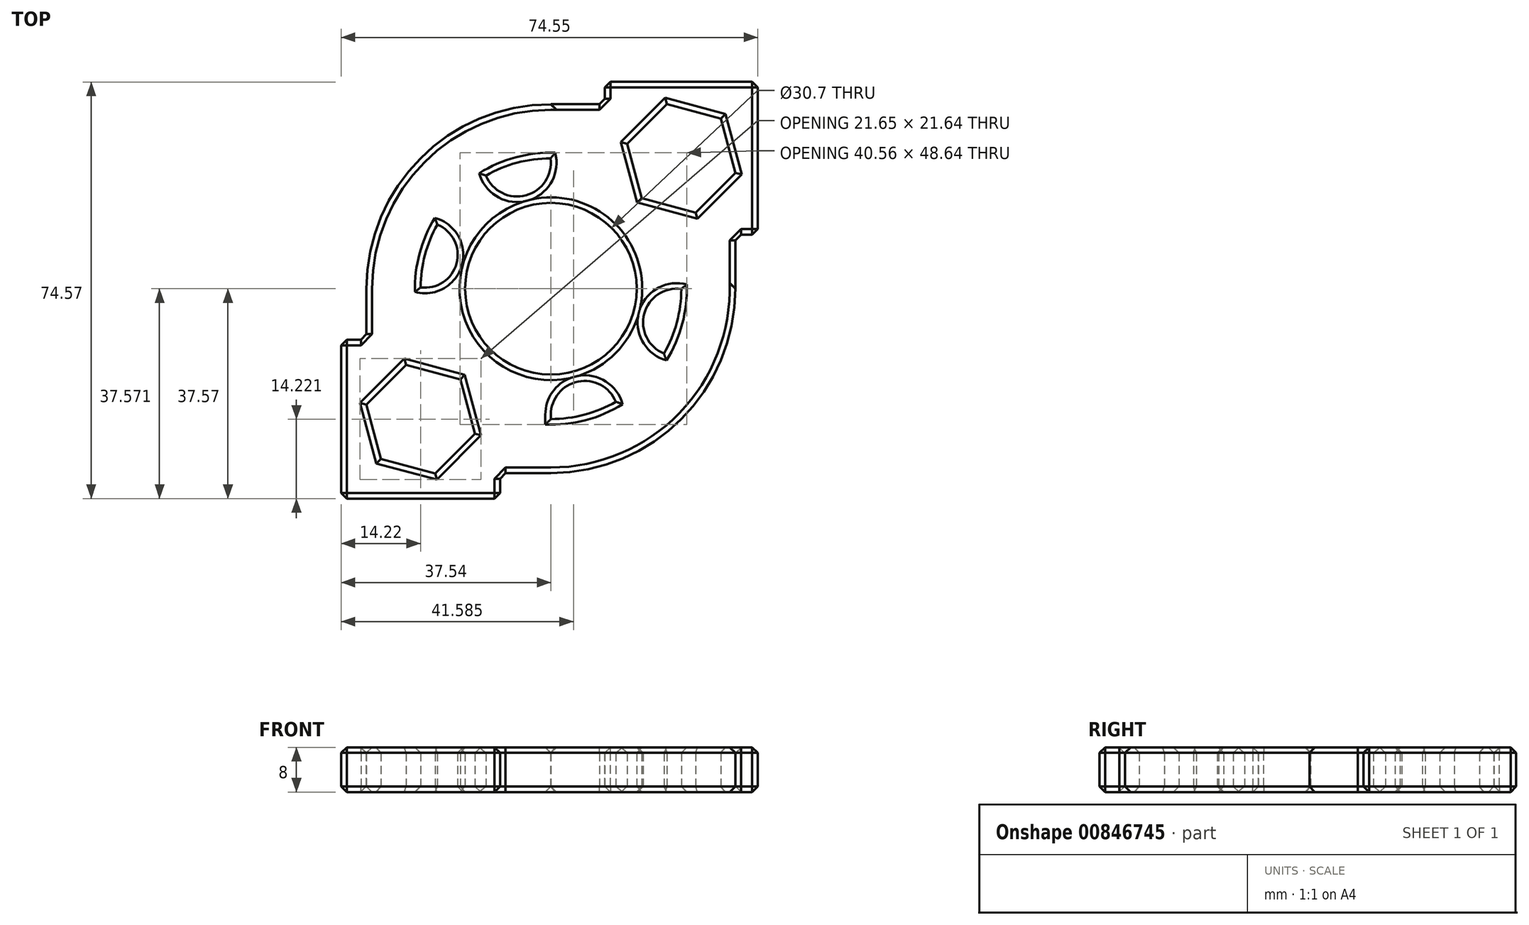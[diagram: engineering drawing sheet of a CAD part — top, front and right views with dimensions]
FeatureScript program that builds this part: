
annotation { "Feature Type Name" : "Feature", "Feature Type Description" : "" }
export const myFeature = defineFeature(function(context is Context, id is Id, definition is map)
    precondition{}
    {
        {
            var Q0;
            Q0=qCreatedBy(makeId("Top.planeOp"),FACE);
            var sketch = newSketch(context, id + "F0", { "sketchPlane" : qUnion([Q0])});
            skCircle(sketch, "E0", {"center": v(0, 0) * mm, "radius": 15.35 * mm});
            skLineSegment(sketch, "E1", {"start": v(0, -33) * mm, "end": v(0, -20.33) * mm});
            skLineSegment(sketch, "E2", {"start": v(0, 16.5) * mm, "end": v(0, 16.5) * mm});
            skCircle(sketch, "E3.cCircle", {"center": v(16.5, 16.5) * mm, "radius": 9.67 * mm, "construction": true});
            skLineSegment(sketch, "E3.0", {"start": v(0, 23.33) * mm, "end": v(0, 33) * mm});
            skLineSegment(sketch, "E3.2", {"start": v(26.17, 16.5) * mm, "end": v(26.17, 16.5) * mm});
            skCircle(sketch, "E4.cCircle", {"center": v(23.34, 23.33) * mm, "radius": 9.67 * mm, "construction": true});
            skLineSegment(sketch, "E4.0", {"start": v(16.5, 26.16) * mm, "end": v(16.5, 26.17) * mm});
            skLineSegment(sketch, "E4.2", {"start": v(30.17, 16.5) * mm, "end": v(30.17, 16.5) * mm});
            skArc(sketch, "E5.cCircle", {"start": v(20.23, -11.62) * mm, "mid": v(-16.5, 16.5) * mm, "end": v(11.62, -20.23) * mm, "construction": true});
            skLineSegment(sketch, "E5.0", {"start": v(16.5, 16.5) * mm, "end": v(16.5, 16.5) * mm});
            skLineSegment(sketch, "E5.1", {"start": v(6.83, -16.5) * mm, "end": v(6.04, -16.5) * mm});
            skCircle(sketch, "E6.cCircle", {"center": v(-16.5, -16.5) * mm, "radius": 23.33 * mm, "construction": true});
            skLineSegment(sketch, "E6.0", {"start": v(0, -20.33) * mm, "end": v(0, -33) * mm});
            skLineSegment(sketch, "E6.1", {"start": v(0, -33) * mm, "end": v(-6.69, -33) * mm});
            skLineSegment(sketch, "E6.3", {"start": v(-33, 0) * mm, "end": v(-23.33, 0) * mm});
            skCircle(sketch, "E7.cCircle", {"center": v(-33.17, -33.43) * mm, "radius": 23.76 * mm, "construction": true});
            skLineSegment(sketch, "E7.0", {"start": v(-16.32, -39.83) * mm, "end": v(-16.32, -39.97) * mm});
            skCircle(sketch, "E8.cCircle", {"center": v(-23.32, -23.35) * mm, "radius": 10.05 * mm, "construction": true});
            skLineSegment(sketch, "E8.0", {"start": v(-16.22, -16.24) * mm, "end": v(-13.61, -25.94) * mm});
            skLineSegment(sketch, "E8.1", {"start": v(-13.61, -25.94) * mm, "end": v(-20.71, -33.05) * mm});
            skLineSegment(sketch, "E8.2", {"start": v(-20.71, -33.05) * mm, "end": v(-30.42, -30.46) * mm});
            skLineSegment(sketch, "E8.3", {"start": v(-30.42, -30.46) * mm, "end": v(-33.03, -20.75) * mm});
            skLineSegment(sketch, "E8.4", {"start": v(-33.03, -20.75) * mm, "end": v(-25.93, -13.64) * mm});
            skLineSegment(sketch, "E8.5", {"start": v(-25.93, -13.64) * mm, "end": v(-16.22, -16.24) * mm});
            skCircle(sketch, "E9.cCircle", {"center": v(23.34, 23.33) * mm, "radius": 10.05 * mm, "construction": true});
            skLineSegment(sketch, "E9.0", {"start": v(16.23, 16.23) * mm, "end": v(13.63, 25.94) * mm});
            skLineSegment(sketch, "E9.1", {"start": v(13.63, 25.94) * mm, "end": v(20.74, 33.04) * mm});
            skLineSegment(sketch, "E9.2", {"start": v(20.74, 33.04) * mm, "end": v(30.44, 30.44) * mm});
            skLineSegment(sketch, "E9.3", {"start": v(30.44, 30.44) * mm, "end": v(33.04, 20.73) * mm});
            skLineSegment(sketch, "E9.4", {"start": v(33.04, 20.73) * mm, "end": v(25.93, 13.62) * mm});
            skLineSegment(sketch, "E9.5", {"start": v(25.93, 13.62) * mm, "end": v(16.23, 16.23) * mm});
            skLineSegment(sketch, "E10.trimOffspring", {"start": v(-33, -6.73) * mm, "end": v(-33, 0) * mm});
            skArc(sketch, "E11.cCircle", {"start": v(-23.33, 0.17) * mm, "mid": v(-27.39, -46.5) * mm, "end": v(-15.3, -1.24) * mm, "construction": true});
            skLineSegment(sketch, "E11.1", {"start": v(-10.33, -39.97) * mm, "end": v(-39.94, -39.99) * mm});
            skLineSegment(sketch, "E11.2", {"start": v(-39.94, -39.99) * mm, "end": v(-39.96, -6.73) * mm});
            skLineSegment(sketch, "E11.3", {"start": v(-39.96, -6.73) * mm, "end": v(-33, -6.73) * mm});
            skLineSegment(sketch, "E12.trimOffspring", {"start": v(-39.95, -16.68) * mm, "end": v(-39.83, -16.68) * mm});
            skLineSegment(sketch, "E13.trimOffspring", {"start": v(-16.22, -16.24) * mm, "end": v(-16.22, -16.24) * mm});
            skPoint(sketch, "E14.orphan", {"position": v(-6.7, -6.71) * mm});
            skLineSegment(sketch, "E15.trimOffspring", {"start": v(16.23, 16.23) * mm, "end": v(16.23, 16.23) * mm});
            skPoint(sketch, "E16.orphan", {"position": v(30.17, 30.17) * mm});
            skCircle(sketch, "E17.cCircle", {"center": v(16.5, 16.5) * mm, "radius": 23.34 * mm, "construction": true});
            skLineSegment(sketch, "E17.0", {"start": v(0, 33) * mm, "end": v(0, 33) * mm});
            skLineSegment(sketch, "E17.1", {"start": v(0, 33) * mm, "end": v(9.67, 33) * mm});
            skLineSegment(sketch, "E17.3", {"start": v(33, 0) * mm, "end": v(33, 0) * mm});
            skCircle(sketch, "E18.cCircle", {"center": v(23.34, 23.33) * mm, "radius": 19.33 * mm, "construction": true});
            skLineSegment(sketch, "E18.1", {"start": v(9.67, 37) * mm, "end": v(37, 37) * mm});
            skLineSegment(sketch, "E18.2", {"start": v(37, 37) * mm, "end": v(37, 9.66) * mm});
            skLineSegment(sketch, "E18.3", {"start": v(37, 9.66) * mm, "end": v(33, 9.66) * mm});
            skPoint(sketch, "E19.orphan", {"position": v(9.67, 9.66) * mm});
            skLineSegment(sketch, "E20.trimOffspring", {"start": v(33, 9.66) * mm, "end": v(33, 0) * mm});
            skPoint(sketch, "E21.orphan", {"position": v(33, 16.5) * mm});
            skLineSegment(sketch, "E22.trimOffspring", {"start": v(9.67, 33) * mm, "end": v(9.67, 37) * mm});
            skLineSegment(sketch, "E23.trimOffspring", {"start": v(16.5, 26.17) * mm, "end": v(16.5, 26.16) * mm});
            skPoint(sketch, "E24.orphan", {"position": v(33, 33) * mm});
            skLineSegment(sketch, "E25.trimOffspring", {"start": v(16.5, 0) * mm, "end": v(16.5, 0) * mm});
            skCircle(sketch, "E26", {"center": v(0, 0) * mm, "radius": 23.33 * mm});
            skArc(sketch, "E27", {"start": v(-1.85, -32.95) * mm, "mid": v(22, 24.6) * mm, "end": v(-32.54, -5.49) * mm});
            skCircle(sketch, "E28", {"center": v(-6.04, 22.54) * mm, "radius": 6.04 * mm});
            skArc(sketch, "E29", {"start": v(-23.33, 0.23) * mm, "mid": v(-16.87, 4.52) * mm, "end": v(-20.32, 11.47) * mm});
            skArc(sketch, "E30", {"start": v(23.33, -0.06) * mm, "mid": v(16.7, -4.48) * mm, "end": v(20.23, -11.62) * mm});
            skArc(sketch, "E31", {"start": v(11.62, -20.23) * mm, "mid": v(1.77, -18.27) * mm, "end": v(3.73, -28.12) * mm});
            skPoint(sketch, "E32.orphan", {"position": v(16.5, -16.5) * mm});
            skPoint(sketch, "E33.orphan", {"position": v(-16.5, 16.5) * mm});
            skLineSegment(sketch, "E34.trimOffspring", {"start": v(0, 22.65) * mm, "end": v(0, 22.43) * mm});
            skPoint(sketch, "E35.start.orphan", {"position": v(0, 33) * mm});
            skCircle(sketch, "E36", {"center": v(-16.22, -16.24) * mm, "radius": 10.05 * mm});
            skLineSegment(sketch, "E37", {"start": v(-6.7, -6.71) * mm, "end": v(-16.22, -16.24) * mm});
            skCircle(sketch, "E38.cCircle", {"center": v(-23.32, -23.35) * mm, "radius": 20.1 * mm, "construction": true});
            skLineSegment(sketch, "E38.0", {"start": v(-9.12, -9.13) * mm, "end": v(-9.1, -23.34) * mm});
            skLineSegment(sketch, "E38.1", {"start": v(-9.1, -37.55) * mm, "end": v(-37.53, -37.57) * mm});
            skLineSegment(sketch, "E38.2", {"start": v(-37.53, -37.57) * mm, "end": v(-37.54, -9.14) * mm});
            skLineSegment(sketch, "E38.3", {"start": v(-37.54, -9.14) * mm, "end": v(-9.12, -9.13) * mm});
            skLineSegment(sketch, "E39", {"start": v(-33, -6.73) * mm, "end": v(-33, -9.14) * mm});
            skLineSegment(sketch, "E40", {"start": v(-6.69, -33) * mm, "end": v(-9.12, -33) * mm});
            skLineSegment(sketch, "E41.trimOffspring", {"start": v(-9.1, -33) * mm, "end": v(-9.1, -37.55) * mm});
            skPoint(sketch, "E42.orphan", {"position": v(-6.68, -39.97) * mm});
            skArc(sketch, "E43.trimOffspring", {"start": v(-31.7, -9.14) * mm, "mid": v(-25.53, -20.9) * mm, "end": v(-15.21, -29.29) * mm});
            skSolve(sketch);
        }
        {
            var Q0;
            {var subQ3=sQuery(id+"F0.wireOp",EDGE,"E8.0");var subQ5=sQuery(id+"F0.wireOp",EDGE,"E8.1");var subQ6=makeQuery(id+"F0.imprint","INTERSECT",VERTEX,{"derivedFrom":[subQ3,subQ5]});Q0=makeQuery(id+"F0.imprint","IMPRINT",FACE,{"disambiguationData":[TD([[makeQuery(id+"F0.imprint","IMPRINT",EDGE,{"disambiguationData":[TD([[subQ6,1.0]])],"derivedFrom":subQ3}),1.0]])]});}
            var Q1;
            {var subQ4=sQuery(id+"F0.wireOp",EDGE,"E27");var subQ5=sQuery(id+"F0.wireOp",EDGE,"E3.0");var subQ6=makeQuery(id+"F0.imprint","INTERSECT",VERTEX,{"derivedFrom":[subQ5,subQ4]});Q1=makeQuery(id+"F0.imprint","IMPRINT",FACE,{"disambiguationData":[TD([[makeQuery(id+"F0.imprint","IMPRINT",EDGE,{"disambiguationData":[TD([[subQ6,1.0]])],"derivedFrom":subQ5}),1.0]])]});}
            var Q2;
            {var subQ1=sQuery(id+"F0.wireOp",EDGE,"E9.0");var subQ7=sQuery(id+"F0.wireOp",EDGE,"E9.1");var subQ9=makeQuery(id+"F0.imprint","INTERSECT",VERTEX,{"derivedFrom":[subQ1,subQ7]});Q2=makeQuery(id+"F0.imprint","IMPRINT",FACE,{"disambiguationData":[TD([[makeQuery(id+"F0.imprint","IMPRINT",EDGE,{"disambiguationData":[TD([[subQ9,1.0]])],"derivedFrom":subQ1}),1.0]])]});}
            var Q3;
            {var subQ4=sQuery(id+"F0.wireOp",EDGE,"E6.1");Q3=makeQuery(id+"F0.imprint","IMPRINT",FACE,{"disambiguationData":[TD([[makeQuery(id+"F0.imprint","IMPRINT",EDGE,{"derivedFrom":subQ4}),-1.0]])]});}
            var Q4;
            {var subQ7=sQuery(id+"F0.wireOp",EDGE,"E9.2");Q4=makeQuery(id+"F0.imprint","IMPRINT",FACE,{"disambiguationData":[TD([[makeQuery(id+"F0.imprint","IMPRINT",EDGE,{"derivedFrom":subQ7}),1.0]])]});}
            var Q5;
            {var subQ4=sQuery(id+"F0.wireOp",EDGE,"E17.3");var subQ6=sQuery(id+"F0.wireOp",EDGE,"E27");var subQ8=makeQuery(id+"F0.imprint","INTERSECT",VERTEX,{"derivedFrom":[subQ4,subQ6]});Q5=makeQuery(id+"F0.imprint","IMPRINT",FACE,{"disambiguationData":[TD([[makeQuery(id+"F0.imprint","IMPRINT",EDGE,{"disambiguationData":[TD([[subQ8,-1.0]])],"derivedFrom":subQ4}),1.0]])]});}
            var Q6;
            {var subQ5=sQuery(id+"F0.wireOp",EDGE,"E27");var subQ7=sQuery(id+"F0.wireOp",EDGE,"E3.3");var subQ9=makeQuery(id+"F0.imprint","INTERSECT",VERTEX,{"derivedFrom":[subQ7,subQ5]});Q6=makeQuery(id+"F0.imprint","IMPRINT",FACE,{"disambiguationData":[TD([[makeQuery(id+"F0.imprint","IMPRINT",EDGE,{"disambiguationData":[TD([[subQ9,-1.0]])],"derivedFrom":subQ7}),-1.0]])]});}
            var Q7;
            Q7=makeQuery(id+"F0.imprint","IMPRINT",FACE,{"disambiguationData":[TD([[makeQuery(id+"F0.imprint","IMPRINT",EDGE,{"derivedFrom":sQuery(id+"F0.wireOp",EDGE,"E0")}),-1.0]])]});
            var Q8;
            {var subQ0=sQuery(id+"F0.wireOp",EDGE,"E28");var subQ1=sQuery(id+"F0.wireOp",EDGE,"E26");var subQ2=makeQuery(id+"F0.imprint","INTERSECT",VERTEX,{"disambiguationData":[OD(0.0)],"derivedFrom":[subQ1,subQ0]});Q8=makeQuery(id+"F0.imprint","IMPRINT",FACE,{"disambiguationData":[TD([[makeQuery(id+"F0.imprint","IMPRINT",EDGE,{"disambiguationData":[TD([[subQ2,-1.0]])],"derivedFrom":subQ1}),-1.0]])]});}
            var Q9;
            {var subQ0=sQuery(id+"F0.wireOp",EDGE,"E9.5");var subQ1=sQuery(id+"F0.wireOp",EDGE,"E9.4");var subQ2=makeQuery(id+"F0.imprint","INTERSECT",VERTEX,{"derivedFrom":[subQ1,subQ0]});Q9=makeQuery(id+"F0.imprint","IMPRINT",FACE,{"disambiguationData":[TD([[makeQuery(id+"F0.imprint","IMPRINT",EDGE,{"disambiguationData":[TD([[subQ2,1.0]])],"derivedFrom":subQ1}),1.0]])]});}
            var Q10;
            {var subQ3=sQuery(id+"F0.wireOp",EDGE,"E43.trimOffspring");var subQ5=sQuery(id+"F0.wireOp",EDGE,"E38.3");var subQ7=makeQuery(id+"F0.imprint","INTERSECT",VERTEX,{"derivedFrom":[subQ5,subQ3]});Q10=makeQuery(id+"F0.imprint","IMPRINT",FACE,{"disambiguationData":[TD([[makeQuery(id+"F0.imprint","IMPRINT",EDGE,{"disambiguationData":[TD([[subQ7,-1.0]])],"derivedFrom":subQ5}),-1.0]])]});}
            var Q11;
            {var subQ1=sQuery(id+"F0.wireOp",EDGE,"E8.5");var subQ3=sQuery(id+"F0.wireOp",EDGE,"E26");var subQ4=makeQuery(id+"F0.imprint","INTERSECT",VERTEX,{"derivedFrom":[subQ1,subQ3]});Q11=makeQuery(id+"F0.imprint","IMPRINT",FACE,{"disambiguationData":[TD([[makeQuery(id+"F0.imprint","IMPRINT",EDGE,{"disambiguationData":[TD([[subQ4,1.0]])],"derivedFrom":subQ3}),-1.0]])]});}
            var Q12;
            {var subQ1=sQuery(id+"F0.wireOp",EDGE,"E6.3");Q12=makeQuery(id+"F0.imprint","IMPRINT",FACE,{"disambiguationData":[TD([[makeQuery(id+"F0.imprint","IMPRINT",EDGE,{"derivedFrom":subQ1}),-1.0]])]});}
            var Q13;
            {var subQ0=sQuery(id+"F0.wireOp",EDGE,"E36");var subQ1=sQuery(id+"F0.wireOp",EDGE,"E26");var subQ2=makeQuery(id+"F0.imprint","INTERSECT",VERTEX,{"disambiguationData":[OD(0.0)],"derivedFrom":[subQ1,subQ0]});Q13=makeQuery(id+"F0.imprint","IMPRINT",FACE,{"disambiguationData":[TD([[makeQuery(id+"F0.imprint","IMPRINT",EDGE,{"disambiguationData":[TD([[subQ2,-1.0]])],"derivedFrom":subQ1}),-1.0]])]});}
            var Q14;
            {var subQ0=sQuery(id+"F0.wireOp",EDGE,"E38.0");var subQ1=sQuery(id+"F0.wireOp",EDGE,"E26");var subQ2=makeQuery(id+"F0.imprint","INTERSECT",VERTEX,{"derivedFrom":[subQ1,subQ0]});Q14=makeQuery(id+"F0.imprint","IMPRINT",FACE,{"disambiguationData":[TD([[makeQuery(id+"F0.imprint","IMPRINT",EDGE,{"disambiguationData":[TD([[subQ2,-1.0]])],"derivedFrom":subQ1}),-1.0]])]});}
            var Q15;
            {var subQ0=sQuery(id+"F0.wireOp",EDGE,"E37");var subQ3=sQuery(id+"F0.wireOp",EDGE,"E0");var subQ4=makeQuery(id+"F0.imprint","INTERSECT",VERTEX,{"derivedFrom":[subQ3,subQ0]});Q15=makeQuery(id+"F0.imprint","IMPRINT",FACE,{"disambiguationData":[TD([[makeQuery(id+"F0.imprint","IMPRINT",EDGE,{"disambiguationData":[TD([[subQ4,-1.0]])],"derivedFrom":subQ3}),-1.0]])]});}
            var Q16;
            {var subQ0=sQuery(id+"F0.wireOp",EDGE,"E8.5");var subQ1=makeQuery(id+"F0.imprint","IMPRINT",VERTEX,{"derivedFrom":subQ0});Q16=makeQuery(id+"F0.imprint","IMPRINT",FACE,{"disambiguationData":[TD([[makeQuery(id+"F0.imprint","IMPRINT",EDGE,{"disambiguationData":[TD([[subQ1,1.0]])],"derivedFrom":subQ0}),1.0]])]});}
            var Q17;
            {var subQ10=sQuery(id+"F0.wireOp",EDGE,"E29");Q17=makeQuery(id+"F0.imprint","IMPRINT",FACE,{"disambiguationData":[TD([[makeQuery(id+"F0.imprint","IMPRINT",EDGE,{"derivedFrom":subQ10}),-1.0]])]});}
            extrude(context, id + "F1", {"entities" : qUnion([Q0, Q1, Q2, Q3, Q4, Q5, Q6, Q7, Q8, Q9, Q10, Q11, Q12, Q13, Q14, Q15, Q16, Q17]), "depth" : 8 * mm, "offsetDistance" : 25 * mm});
        }
        {
            var Q0;
            Q0=makeQuery(id+"F1.opExtrude","CAP_FACE",FACE,{"disambiguationData":[OSD([sQuery(id+"F0.wireOp",EDGE,"E0"),sQuery(id+"F0.wireOp",EDGE,"E6.0"),sQuery(id+"F0.wireOp",EDGE,"E6.1"),sQuery(id+"F0.wireOp",EDGE,"E8.0"),sQuery(id+"F0.wireOp",EDGE,"E8.1"),sQuery(id+"F0.wireOp",EDGE,"E8.2"),sQuery(id+"F0.wireOp",EDGE,"E8.3"),sQuery(id+"F0.wireOp",EDGE,"E8.4"),sQuery(id+"F0.wireOp",EDGE,"E8.5"),sQuery(id+"F0.wireOp",EDGE,"E9.0"),sQuery(id+"F0.wireOp",EDGE,"E9.1"),sQuery(id+"F0.wireOp",EDGE,"E9.2"),sQuery(id+"F0.wireOp",EDGE,"E9.3"),sQuery(id+"F0.wireOp",EDGE,"E9.4"),sQuery(id+"F0.wireOp",EDGE,"E9.5"),sQuery(id+"F0.wireOp",EDGE,"E10.trimOffspring"),sQuery(id+"F0.wireOp",EDGE,"E17.0"),sQuery(id+"F0.wireOp",EDGE,"E17.1"),sQuery(id+"F0.wireOp",EDGE,"E17.3"),sQuery(id+"F0.wireOp",EDGE,"E18.1"),sQuery(id+"F0.wireOp",EDGE,"E18.2"),sQuery(id+"F0.wireOp",EDGE,"E18.3"),sQuery(id+"F0.wireOp",EDGE,"E20.trimOffspring"),sQuery(id+"F0.wireOp",EDGE,"E22.trimOffspring"),sQuery(id+"F0.wireOp",EDGE,"E26"),sQuery(id+"F0.wireOp",EDGE,"E27"),sQuery(id+"F0.wireOp",EDGE,"E28"),sQuery(id+"F0.wireOp",EDGE,"E29"),sQuery(id+"F0.wireOp",EDGE,"E30"),sQuery(id+"F0.wireOp",EDGE,"E31"),sQuery(id+"F0.wireOp",EDGE,"E38.1"),sQuery(id+"F0.wireOp",EDGE,"E38.2"),sQuery(id+"F0.wireOp",EDGE,"E38.3"),sQuery(id+"F0.wireOp",EDGE,"E39"),sQuery(id+"F0.wireOp",EDGE,"E40"),sQuery(id+"F0.wireOp",EDGE,"E41.trimOffspring")])],"isStart":true});
            var Q1;
            Q1=makeQuery(id+"F1.opExtrude","CAP_FACE",FACE,{"disambiguationData":[OSD([sQuery(id+"F0.wireOp",EDGE,"E0"),sQuery(id+"F0.wireOp",EDGE,"E6.0"),sQuery(id+"F0.wireOp",EDGE,"E6.1"),sQuery(id+"F0.wireOp",EDGE,"E8.0"),sQuery(id+"F0.wireOp",EDGE,"E8.1"),sQuery(id+"F0.wireOp",EDGE,"E8.2"),sQuery(id+"F0.wireOp",EDGE,"E8.3"),sQuery(id+"F0.wireOp",EDGE,"E8.4"),sQuery(id+"F0.wireOp",EDGE,"E8.5"),sQuery(id+"F0.wireOp",EDGE,"E9.0"),sQuery(id+"F0.wireOp",EDGE,"E9.1"),sQuery(id+"F0.wireOp",EDGE,"E9.2"),sQuery(id+"F0.wireOp",EDGE,"E9.3"),sQuery(id+"F0.wireOp",EDGE,"E9.4"),sQuery(id+"F0.wireOp",EDGE,"E9.5"),sQuery(id+"F0.wireOp",EDGE,"E10.trimOffspring"),sQuery(id+"F0.wireOp",EDGE,"E17.0"),sQuery(id+"F0.wireOp",EDGE,"E17.1"),sQuery(id+"F0.wireOp",EDGE,"E17.3"),sQuery(id+"F0.wireOp",EDGE,"E18.1"),sQuery(id+"F0.wireOp",EDGE,"E18.2"),sQuery(id+"F0.wireOp",EDGE,"E18.3"),sQuery(id+"F0.wireOp",EDGE,"E20.trimOffspring"),sQuery(id+"F0.wireOp",EDGE,"E22.trimOffspring"),sQuery(id+"F0.wireOp",EDGE,"E26"),sQuery(id+"F0.wireOp",EDGE,"E27"),sQuery(id+"F0.wireOp",EDGE,"E28"),sQuery(id+"F0.wireOp",EDGE,"E29"),sQuery(id+"F0.wireOp",EDGE,"E30"),sQuery(id+"F0.wireOp",EDGE,"E31"),sQuery(id+"F0.wireOp",EDGE,"E38.1"),sQuery(id+"F0.wireOp",EDGE,"E38.2"),sQuery(id+"F0.wireOp",EDGE,"E38.3"),sQuery(id+"F0.wireOp",EDGE,"E39"),sQuery(id+"F0.wireOp",EDGE,"E40"),sQuery(id+"F0.wireOp",EDGE,"E41.trimOffspring")])],"isStart":false});
            var Q2;
            Q2=makeQuery(id+"F1.opExtrude","SWEPT_EDGE",EDGE,{"disambiguationData":[OSD([sQuery(id+"F0.wireOp",EDGE,"E18.1"),sQuery(id+"F0.wireOp",EDGE,"E18.2")])]});
            var Q3;
            Q3=makeQuery(id+"F1.opExtrude","SWEPT_EDGE",EDGE,{"disambiguationData":[OSD([sQuery(id+"F0.wireOp",EDGE,"E18.1"),sQuery(id+"F0.wireOp",EDGE,"E22.trimOffspring")])]});
            var Q4;
            Q4=makeQuery(id+"F1.opExtrude","SWEPT_EDGE",EDGE,{"disambiguationData":[OSD([sQuery(id+"F0.wireOp",EDGE,"E17.1"),sQuery(id+"F0.wireOp",EDGE,"E22.trimOffspring")])]});
            var Q5;
            Q5=makeQuery(id+"F1.opExtrude","SWEPT_EDGE",EDGE,{"disambiguationData":[OSD([sQuery(id+"F0.wireOp",EDGE,"E18.3"),sQuery(id+"F0.wireOp",EDGE,"E20.trimOffspring")])]});
            var Q6;
            Q6=makeQuery(id+"F1.opExtrude","SWEPT_EDGE",EDGE,{"disambiguationData":[OSD([sQuery(id+"F0.wireOp",EDGE,"E18.2"),sQuery(id+"F0.wireOp",EDGE,"E18.3")])]});
            var Q7;
            Q7=makeQuery(id+"F1.opExtrude","SWEPT_EDGE",EDGE,{"disambiguationData":[OSD([sQuery(id+"F0.wireOp",EDGE,"E40"),sQuery(id+"F0.wireOp",EDGE,"E41.trimOffspring")])]});
            var Q8;
            Q8=makeQuery(id+"F1.opExtrude","SWEPT_EDGE",EDGE,{"disambiguationData":[OSD([sQuery(id+"F0.wireOp",EDGE,"E38.1"),sQuery(id+"F0.wireOp",EDGE,"E41.trimOffspring")])]});
            var Q9;
            Q9=makeQuery(id+"F1.opExtrude","SWEPT_EDGE",EDGE,{"disambiguationData":[OSD([sQuery(id+"F0.wireOp",EDGE,"E38.1"),sQuery(id+"F0.wireOp",EDGE,"E38.2")])]});
            var Q10;
            Q10=makeQuery(id+"F1.opExtrude","SWEPT_EDGE",EDGE,{"disambiguationData":[OSD([sQuery(id+"F0.wireOp",EDGE,"E38.2"),sQuery(id+"F0.wireOp",EDGE,"E38.3")])]});
            var Q11;
            Q11=makeQuery(id+"F1.opExtrude","SWEPT_EDGE",EDGE,{"disambiguationData":[OSD([sQuery(id+"F0.wireOp",EDGE,"E38.3"),sQuery(id+"F0.wireOp",EDGE,"E39")])]});
            var Q12;
            Q12=makeQuery(id+"F1.opExtrude","CAP_EDGE",EDGE,{"disambiguationData":[OSD([sQuery(id+"F0.wireOp",EDGE,"E29")])],"isStart":false});
            chamfer(context, id + "F2", {"entities" : qUnion([Q0, Q1, Q2, Q3, Q4, Q5, Q6, Q7, Q8, Q9, Q10, Q11, Q12]), "width" : 1 * mm, "tangentPropagation" : true});
        }
    });
